# Revit family: VFB_FF108_Linear Gap Seals
name_source: partatom
category: Specialty Equipment
revit_build: Autodesk Revit 2015 (Build: 20160512_0715(x64)
units: mm (PartAtom-declared; Revit-internal decimal feet)

## types (12) — shared parameters
IFC Classification = Building Element Proxy
Manufacturer = Tenmat ltd
Material/Grade = Intumescent Material
Performance = BS EN 1366-3:2009 & BS 476, ETA-12/0332, 1224-CPR-0341, CE Marked
URL = https://www.tenmat.com
Youtube Clip = https://www.youtube.com

## per-type parameters (varying)
| type | 2 Seals | Depth | Description | Fire Rating - Floors | Fire Rating -Walls | Maximum Gap | Minimum Gap | Tenmat Item Number | Width |
| 15x15 - 1 SEAL | No | 15 mm  [stored 0.0492126 ft] | FF108 25x20mm Linear Gap Seal - 2 Seals | E240/EI180 | E240/EI120 | 13mm | 7.5mm | I108MP01500015100000 | 15 mm  [stored 0.0492126 ft] |
| 25x20 - 1 SEAL | No | 20 mm  [stored 0.0656168 ft] | FF108 25x20mm Linear Gap Seal - 1 Seal | E240/EI30 | E240/EI30 | 22mm | 13mm | I108MP02500020100000 | 25 mm  [stored 0.082021 ft] |
| 30x15 - 2 SEALS | Yes | 15 mm  [stored 0.0492126 ft] | FF108 30x15mm Linear Gap Seal - 2 Seals | E240/EI180 | E240/EI180 | 25mm | 15mm | I108MP03000015100000 | 30 mm  [stored 0.0984252 ft] |
| 40x20 - 1 SEAL | No | 20 mm  [stored 0.0656168 ft] | FF108 40x20mm Linear Gap Seal - 1 Seal | E240/EI30 | E240/EI30 | 35mm | 22mm | I108MP04000020100001 | 40 mm  [stored 0.131234 ft] |
| 60x40 - 2 SEALS | Yes | 40 mm  [stored 0.131234 ft] | FF108 60x40mm Linear Gap Seal - 2 Seals | E240/EI180 | E240/EI120 | 50mm | 35mm | I108MP06000040100000 | 60 mm  [stored 0.19685 ft] |
| 60x45 - 1 SEAL | No | 45 mm  [stored 0.147638 ft] | FF108 60x45mm Linear Gap Seal - 1 Seal | E240/EI45 | E240/EI45 | 50mm | 35mm | I108MP06000045100001 | 60 mm  [stored 0.19685 ft] |
| 85x40 - 2 SEALS | Yes | 40 mm  [stored 0.131234 ft] | FF108 85x40mm Linear Gap Seal - 2 Seals | E240/EI180 | E240/EI120 | 70mm | 50mm | I108MP08500040100000 | 85 mm  [stored 0.278871 ft] |
| 85x45 - 1 SEAL | No | 45 mm  [stored 0.147638 ft] | FF108 85x45mm Linear Gap Seal - 1 Seal | E240/EI45 | E240/EI45 | 70mm | 50mm | I108MP08500045100000 | 85 mm  [stored 0.278871 ft] |
| 120x50 - 2 SEALS | Yes | 50 mm  [stored 0.164042 ft] | FF108 120x50mm Linear Gap Seal - 2 Seals | E240/EI180 | E240/EI180 | 100mm | 70mm | I108MP12000050100000 | 120 mm  [stored 0.393701 ft] |
| 120x60 - 1 SEAL | No | 60 mm  [stored 0.19685 ft] | FF108 120x60mm Linear Gap Seal - 1 Seal | E240/EI45 | E240/EI45 | 100mm | 70mm | I108MP12000060100000 | 120 mm  [stored 0.393701 ft] |
| 25x20 - 2 SEALS | Yes | 20 mm  [stored 0.0656168 ft] | FF108 25x20mm Linear Gap Seal - 2 Seals | E240/EI180 | E240/EI120 | 22mm | 13mm | I108MP02500020100000 | 25 mm  [stored 0.082021 ft] |
| 40x20 - 2 SEALS | Yes | 20 mm  [stored 0.0656168 ft] | FF108 40x20mm Linear Gap Seal - 2 Seals | E240/EI180 | E240/EI120 | 35mm | 22mm | I108MP04000020100001 | 40 mm  [stored 0.131234 ft] |

note: [stored X ft] marks values corroborated as IEEE doubles in the binary element streams (Revit-internal decimal feet)

## geometry (parser evidence)
native form markers: Blend x2, Sweep x9
no freeform markers — native parametric forms only
